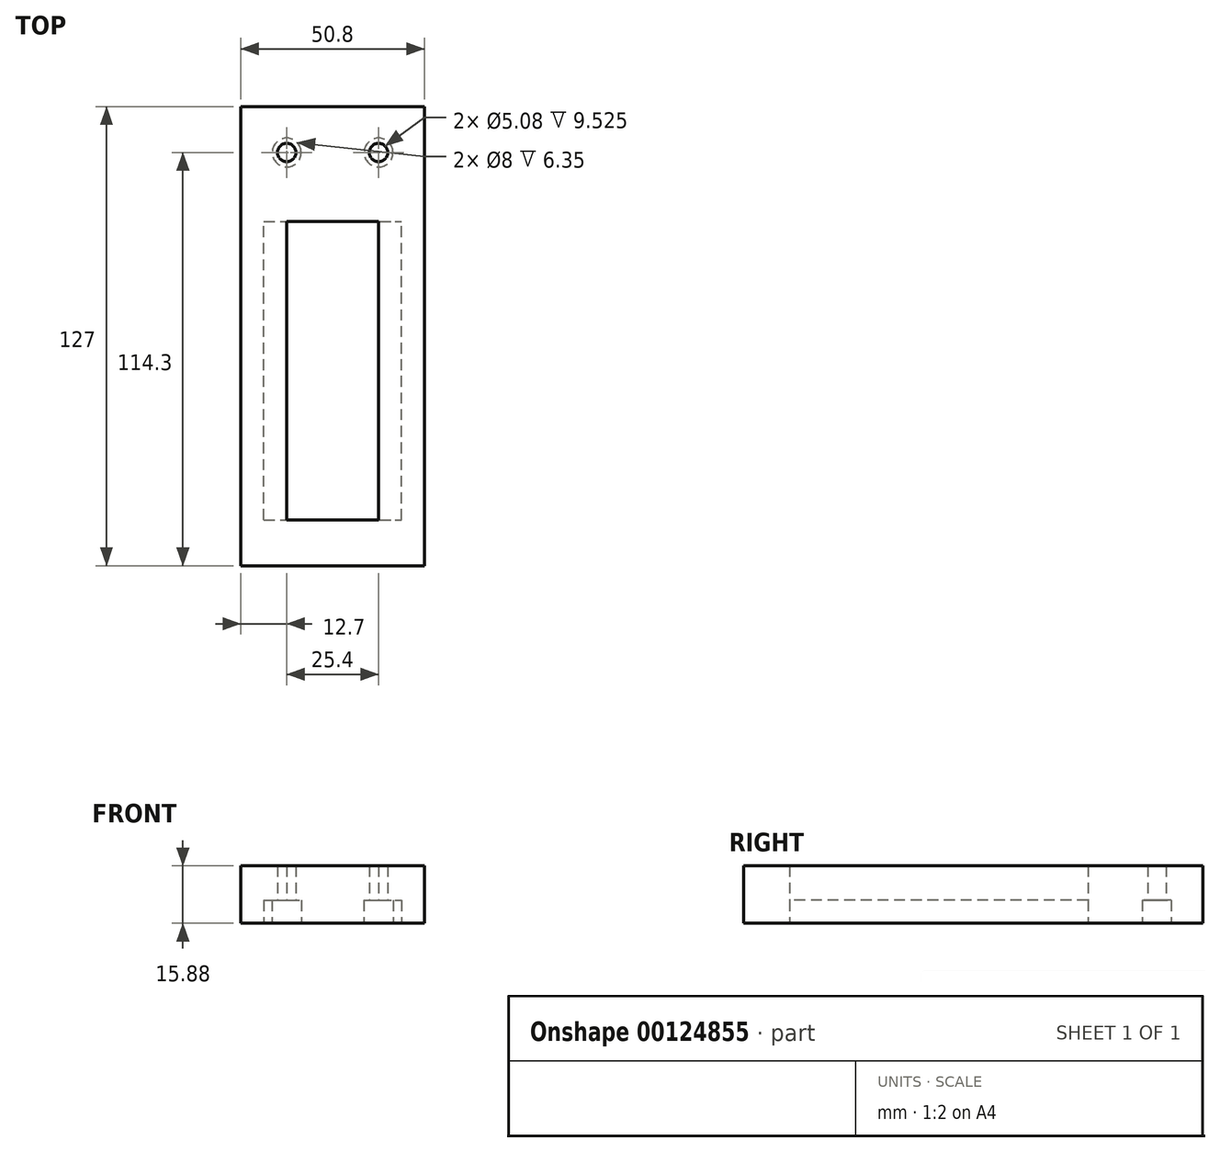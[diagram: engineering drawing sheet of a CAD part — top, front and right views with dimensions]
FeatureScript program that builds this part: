
annotation { "Feature Type Name" : "Feature", "Feature Type Description" : "" }
export const myFeature = defineFeature(function(context is Context, id is Id, definition is map)
    precondition{}
    {
        {
            var Q0;
            Q0=qCreatedBy(makeId("Top.planeOp"),FACE);
            var sketch = newSketch(context, id + "F0", { "sketchPlane" : qUnion([Q0])});
            skLineSegment(sketch, "E0.bottom", {"start": v(0, 0) * mm, "end": v(50.8, 0) * mm});
            skLineSegment(sketch, "E0.top", {"start": v(0, 127) * mm, "end": v(50.8, 127) * mm});
            skLineSegment(sketch, "E0.left", {"start": v(0, 0) * mm, "end": v(0, 127) * mm});
            skLineSegment(sketch, "E0.right", {"start": v(50.8, 0) * mm, "end": v(50.8, 127) * mm});
            skLineSegment(sketch, "E1.bottom", {"start": v(12.7, 95.25) * mm, "end": v(38.1, 95.25) * mm});
            skLineSegment(sketch, "E1.top", {"start": v(12.7, 12.7) * mm, "end": v(38.1, 12.7) * mm});
            skLineSegment(sketch, "E1.left", {"start": v(12.7, 95.25) * mm, "end": v(12.7, 12.7) * mm});
            skLineSegment(sketch, "E1.right", {"start": v(38.1, 95.25) * mm, "end": v(38.1, 12.7) * mm});
            skLineSegment(sketch, "E2", {"start": v(25.4, 117.75) * mm, "end": v(25.4, -21.63) * mm, "construction": true});
            skPoint(sketch, "E2.endSnap0", {"position": v(25.4, 12.7) * mm});
            skSolve(sketch);
        }
        {
            var Q0;
            Q0=makeQuery(id+"F0.imprint","IMPRINT",FACE,{"disambiguationData":[TD([[makeQuery(id+"F0.imprint","IMPRINT",EDGE,{"derivedFrom":sQuery(id+"F0.wireOp",EDGE,"E0.bottom")}),1.0]])]});
            extrude(context, id + "F1", {"entities" : qUnion([Q0]), "depth" : 15.88 * mm});
        }
        {
            var Q0;
            Q0=makeQuery(id+"F1.opExtrude","CAP_FACE",FACE,{"disambiguationData":[OSD([sQuery(id+"F0.wireOp",EDGE,"E0.bottom"),sQuery(id+"F0.wireOp",EDGE,"E0.top"),sQuery(id+"F0.wireOp",EDGE,"E0.left"),sQuery(id+"F0.wireOp",EDGE,"E0.right"),sQuery(id+"F0.wireOp",EDGE,"E1.bottom"),sQuery(id+"F0.wireOp",EDGE,"E1.top"),sQuery(id+"F0.wireOp",EDGE,"E1.left"),sQuery(id+"F0.wireOp",EDGE,"E1.right")])],"isStart":true});
            var sketch = newSketch(context, id + "F2", { "sketchPlane" : qUnion([Q0])});
            skLineSegment(sketch, "E3.bottom", {"start": v(6.35, -12.7) * mm, "end": v(44.45, -12.7) * mm});
            skLineSegment(sketch, "E3.top", {"start": v(6.35, -95.25) * mm, "end": v(44.45, -95.25) * mm});
            skLineSegment(sketch, "E3.left", {"start": v(6.35, -12.7) * mm, "end": v(6.35, -95.25) * mm});
            skLineSegment(sketch, "E3.right", {"start": v(44.45, -12.7) * mm, "end": v(44.45, -95.25) * mm});
            skLineSegment(sketch, "E4", {"start": v(25.4, -132.08) * mm, "end": v(25.4, 24.51) * mm, "construction": true});
            skSolve(sketch);
        }
        {
            var Q0;
            {var subQ2=sQuery(id+"F2.wireOp",EDGE,"E3.right");Q0=makeQuery(id+"F2.imprint","IMPRINT",FACE,{"disambiguationData":[TD([[makeQuery(id+"F2.imprint","IMPRINT",EDGE,{"derivedFrom":subQ2}),-1.0]])]});}
            var Q1;
            {var subQ2=sQuery(id+"F2.wireOp",EDGE,"E3.left");Q1=makeQuery(id+"F2.imprint","IMPRINT",FACE,{"disambiguationData":[TD([[makeQuery(id+"F2.imprint","IMPRINT",EDGE,{"derivedFrom":subQ2}),1.0]])]});}
            extrude(context, id + "F3", {"entities" : qUnion([Q0, Q1]), "operationType" : NewBodyOperationType.REMOVE, "oppositeDirection" : true, "depth" : 6.35 * mm});
        }
        {
            var Q0;
            Q0=makeQuery(id+"F1.opExtrude","CAP_FACE",FACE,{"disambiguationData":[OSD([sQuery(id+"F0.wireOp",EDGE,"E0.bottom"),sQuery(id+"F0.wireOp",EDGE,"E0.top"),sQuery(id+"F0.wireOp",EDGE,"E0.left"),sQuery(id+"F0.wireOp",EDGE,"E0.right"),sQuery(id+"F0.wireOp",EDGE,"E1.bottom"),sQuery(id+"F0.wireOp",EDGE,"E1.top"),sQuery(id+"F0.wireOp",EDGE,"E1.left"),sQuery(id+"F0.wireOp",EDGE,"E1.right")])],"isStart":true});
            var sketch = newSketch(context, id + "F4", { "sketchPlane" : qUnion([Q0])});
            skCircle(sketch, "E5", {"center": v(38.1, -114.3) * mm, "radius": 2.54 * mm});
            skCircle(sketch, "E6", {"center": v(12.7, -114.3) * mm, "radius": 2.54 * mm});
            skLineSegment(sketch, "E7", {"start": v(25.4, -12.7) * mm, "end": v(25.4, -99.23) * mm, "construction": true});
            skPoint(sketch, "E7.endSnap0", {"position": v(25.4, -95.25) * mm});
            skCircle(sketch, "E8", {"center": v(38.1, -114.3) * mm, "radius": 4 * mm});
            skCircle(sketch, "E9", {"center": v(12.7, -114.3) * mm, "radius": 4 * mm});
            skSolve(sketch);
        }
        {
            var Q0;
            Q0=makeQuery(id+"F4.imprint","IMPRINT",FACE,{"disambiguationData":[TD([[makeQuery(id+"F4.imprint","IMPRINT",EDGE,{"derivedFrom":sQuery(id+"F4.wireOp",EDGE,"E5")}),1.0]])]});
            var Q1;
            Q1=makeQuery(id+"F4.imprint","IMPRINT",FACE,{"disambiguationData":[TD([[makeQuery(id+"F4.imprint","IMPRINT",EDGE,{"derivedFrom":sQuery(id+"F4.wireOp",EDGE,"E6")}),1.0]])]});
            extrude(context, id + "F5", {"entities" : qUnion([Q0, Q1]), "operationType" : NewBodyOperationType.REMOVE, "endBound" : BoundingType.THROUGH_ALL, "oppositeDirection" : true, "depth" : 25.4 * mm});
        }
        {
            var Q0;
            Q0=makeQuery(id+"F4.imprint","IMPRINT",FACE,{"disambiguationData":[TD([[makeQuery(id+"F4.imprint","IMPRINT",EDGE,{"derivedFrom":sQuery(id+"F4.wireOp",EDGE,"E5")}),-1.0]])]});
            var Q1;
            Q1=makeQuery(id+"F4.imprint","IMPRINT",FACE,{"disambiguationData":[TD([[makeQuery(id+"F4.imprint","IMPRINT",EDGE,{"derivedFrom":sQuery(id+"F4.wireOp",EDGE,"E6")}),-1.0]])]});
            extrude(context, id + "F6", {"entities" : qUnion([Q0, Q1]), "operationType" : NewBodyOperationType.REMOVE, "oppositeDirection" : true, "depth" : 6.35 * mm});
        }
    });
